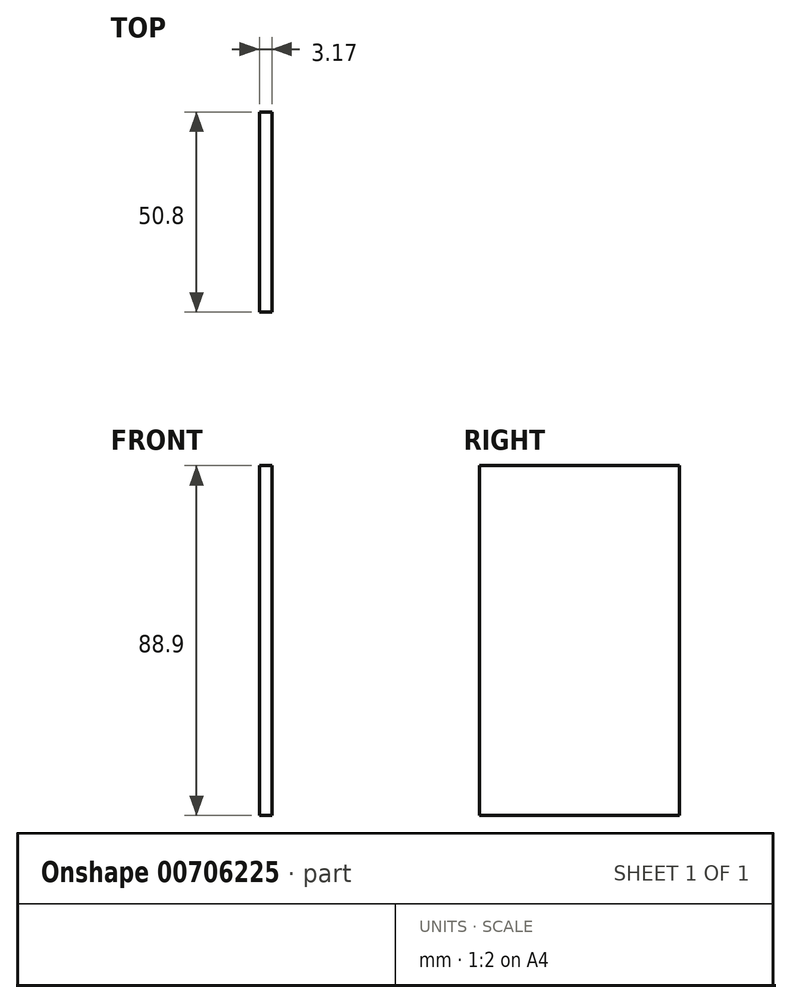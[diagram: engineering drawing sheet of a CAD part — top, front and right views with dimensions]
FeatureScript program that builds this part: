
annotation { "Feature Type Name" : "Feature", "Feature Type Description" : "" }
export const myFeature = defineFeature(function(context is Context, id is Id, definition is map)
    precondition{}
    {
        {
            var Q0;
            Q0=qCreatedBy(makeId("Right.planeOp"),FACE);
            var sketch = newSketch(context, id + "F0", { "sketchPlane" : qUnion([Q0])});
            skLineSegment(sketch, "E0.bottom", {"start": v(-23, 33.78) * mm, "end": v(27.8, 33.78) * mm});
            skLineSegment(sketch, "E0.top", {"start": v(-23, -55.12) * mm, "end": v(27.8, -55.12) * mm});
            skLineSegment(sketch, "E0.left", {"start": v(-23, 33.78) * mm, "end": v(-23, -55.12) * mm});
            skLineSegment(sketch, "E0.right", {"start": v(27.8, 33.78) * mm, "end": v(27.8, -55.12) * mm});
            skSolve(sketch);
        }
        {
            var Q0;
            Q0 = qSketchRegion(id + "F0", true);
            extrude(context, id + "F1", {"entities" : qUnion([Q0]), "depth" : 3.17 * mm, "offsetDistance" : 25.4 * mm});
        }
    });
